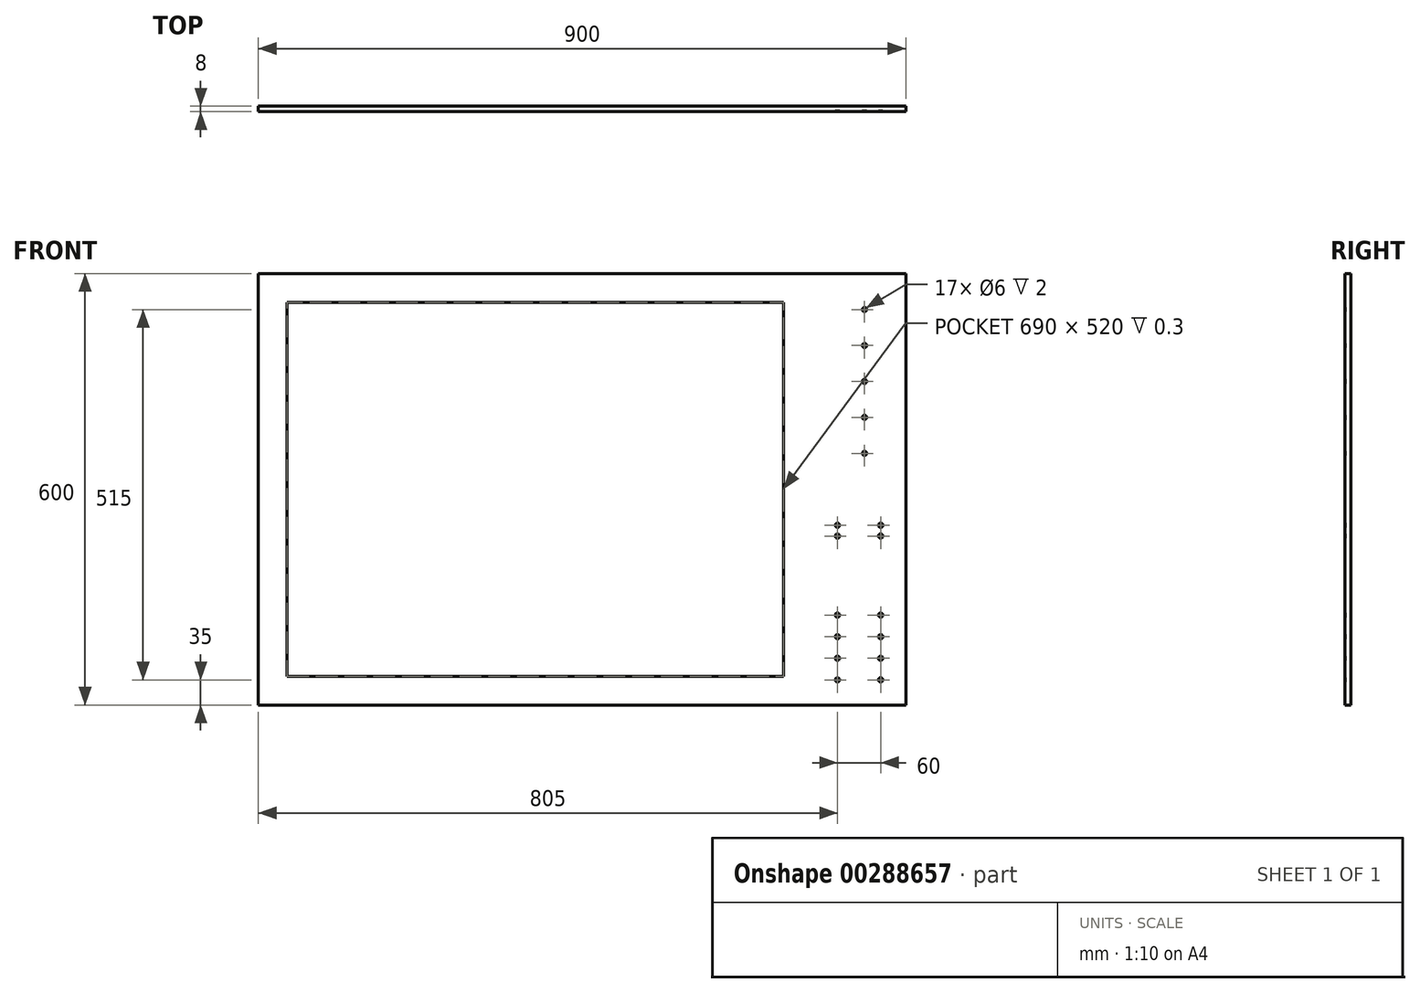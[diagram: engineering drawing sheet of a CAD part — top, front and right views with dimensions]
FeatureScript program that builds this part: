
annotation { "Feature Type Name" : "Feature", "Feature Type Description" : "" }
export const myFeature = defineFeature(function(context is Context, id is Id, definition is map)
    precondition{}
    {
        {
            var Q0;
            Q0=qCreatedBy(makeId("Front.planeOp"),FACE);
            var sketch = newSketch(context, id + "F0", { "sketchPlane" : qUnion([Q0])});
            skLineSegment(sketch, "E0.bottom", {"start": v(450, 300) * mm, "end": v(-450, 300) * mm});
            skLineSegment(sketch, "E0.top", {"start": v(450, -300) * mm, "end": v(-450, -300) * mm});
            skLineSegment(sketch, "E0.left", {"start": v(450, 300) * mm, "end": v(450, -300) * mm});
            skLineSegment(sketch, "E0.right", {"start": v(-450, 300) * mm, "end": v(-450, -300) * mm});
            skPoint(sketch, "E0.middle", {"position": v(0, 0) * mm});
            skSolve(sketch);
        }
        {
            var Q0;
            Q0=makeQuery(id+"F0.imprint","IMPRINT",FACE,{"disambiguationData":[TD([[makeQuery(id+"F0.imprint","IMPRINT",EDGE,{"derivedFrom":sQuery(id+"F0.wireOp",EDGE,"E0.bottom")}),1.0]])]});
            extrude(context, id + "F1", {"entities" : qUnion([Q0]), "depth" : 8 * mm, "offsetDistance" : 25 * mm});
        }
        {
            var Q0;
            Q0=makeQuery(id+"F1.opExtrude","CAP_FACE",FACE,{"disambiguationData":[OSD([sQuery(id+"F0.wireOp",EDGE,"E0.bottom"),sQuery(id+"F0.wireOp",EDGE,"E0.top"),sQuery(id+"F0.wireOp",EDGE,"E0.left"),sQuery(id+"F0.wireOp",EDGE,"E0.right")])],"isStart":false});
            var sketch = newSketch(context, id + "F2", { "sketchPlane" : qUnion([Q0])});
            skLineSegment(sketch, "E1.bottom", {"start": v(280, 260) * mm, "end": v(-410, 260) * mm});
            skLineSegment(sketch, "E1.top", {"start": v(280, -260) * mm, "end": v(-410, -260) * mm});
            skLineSegment(sketch, "E1.left", {"start": v(280, 260) * mm, "end": v(280, -260) * mm});
            skLineSegment(sketch, "E1.right", {"start": v(-410, 260) * mm, "end": v(-410, -260) * mm});
            skPoint(sketch, "E1.middle", {"position": v(-65, 0) * mm});
            skSolve(sketch);
        }
        {
            var Q0;
            Q0=makeQuery(id+"F2.imprint","IMPRINT",FACE,{"disambiguationData":[TD([[makeQuery(id+"F2.imprint","IMPRINT",EDGE,{"derivedFrom":sQuery(id+"F2.wireOp",EDGE,"E1.bottom")}),1.0]])]});
            extrude(context, id + "F3", {"entities" : qUnion([Q0]), "operationType" : NewBodyOperationType.REMOVE, "oppositeDirection" : true, "depth" : 0.3 * mm, "offsetDistance" : 25 * mm});
        }
        {
            var Q0;
            Q0=makeQuery(id+"F1.opExtrude","CAP_FACE",FACE,{"disambiguationData":[OSD([sQuery(id+"F0.wireOp",EDGE,"E0.bottom"),sQuery(id+"F0.wireOp",EDGE,"E0.top"),sQuery(id+"F0.wireOp",EDGE,"E0.left"),sQuery(id+"F0.wireOp",EDGE,"E0.right")])],"isStart":false});
            var sketch = newSketch(context, id + "F4", { "sketchPlane" : qUnion([Q0])});
            skCircle(sketch, "E2", {"center": v(392.5, 100) * mm, "radius": 3 * mm});
            skCircle(sketch, "E3", {"center": v(392.5, 150) * mm, "radius": 3 * mm});
            skCircle(sketch, "E4", {"center": v(415, -65) * mm, "radius": 3 * mm});
            skCircle(sketch, "E5", {"center": v(392.5, 50) * mm, "radius": 3 * mm});
            skCircle(sketch, "E6", {"center": v(355, -50) * mm, "radius": 3 * mm});
            skCircle(sketch, "E7", {"center": v(415, -50) * mm, "radius": 3 * mm});
            skCircle(sketch, "E8", {"center": v(415, -175) * mm, "radius": 3 * mm});
            skCircle(sketch, "E9", {"center": v(415, -205) * mm, "radius": 3 * mm});
            skCircle(sketch, "E10", {"center": v(415, -235) * mm, "radius": 3 * mm});
            skCircle(sketch, "E11", {"center": v(415, -265) * mm, "radius": 3 * mm});
            skCircle(sketch, "E12", {"center": v(355, -265) * mm, "radius": 3 * mm});
            skCircle(sketch, "E13", {"center": v(355, -65) * mm, "radius": 3 * mm});
            skCircle(sketch, "E14", {"center": v(355, -175) * mm, "radius": 3 * mm});
            skCircle(sketch, "E15", {"center": v(355, -205) * mm, "radius": 3 * mm});
            skCircle(sketch, "E16", {"center": v(355, -235) * mm, "radius": 3 * mm});
            skCircle(sketch, "E17", {"center": v(392.5, 200) * mm, "radius": 3 * mm});
            skCircle(sketch, "E18", {"center": v(392.5, 250) * mm, "radius": 3 * mm});
            skSolve(sketch);
        }
        {
            var Q0;
            Q0 = qSketchRegion(id + "F4", true);
            extrude(context, id + "F5", {"entities" : qUnion([Q0]), "operationType" : NewBodyOperationType.REMOVE, "oppositeDirection" : true, "depth" : 2 * mm, "offsetDistance" : 25 * mm});
        }
    });
